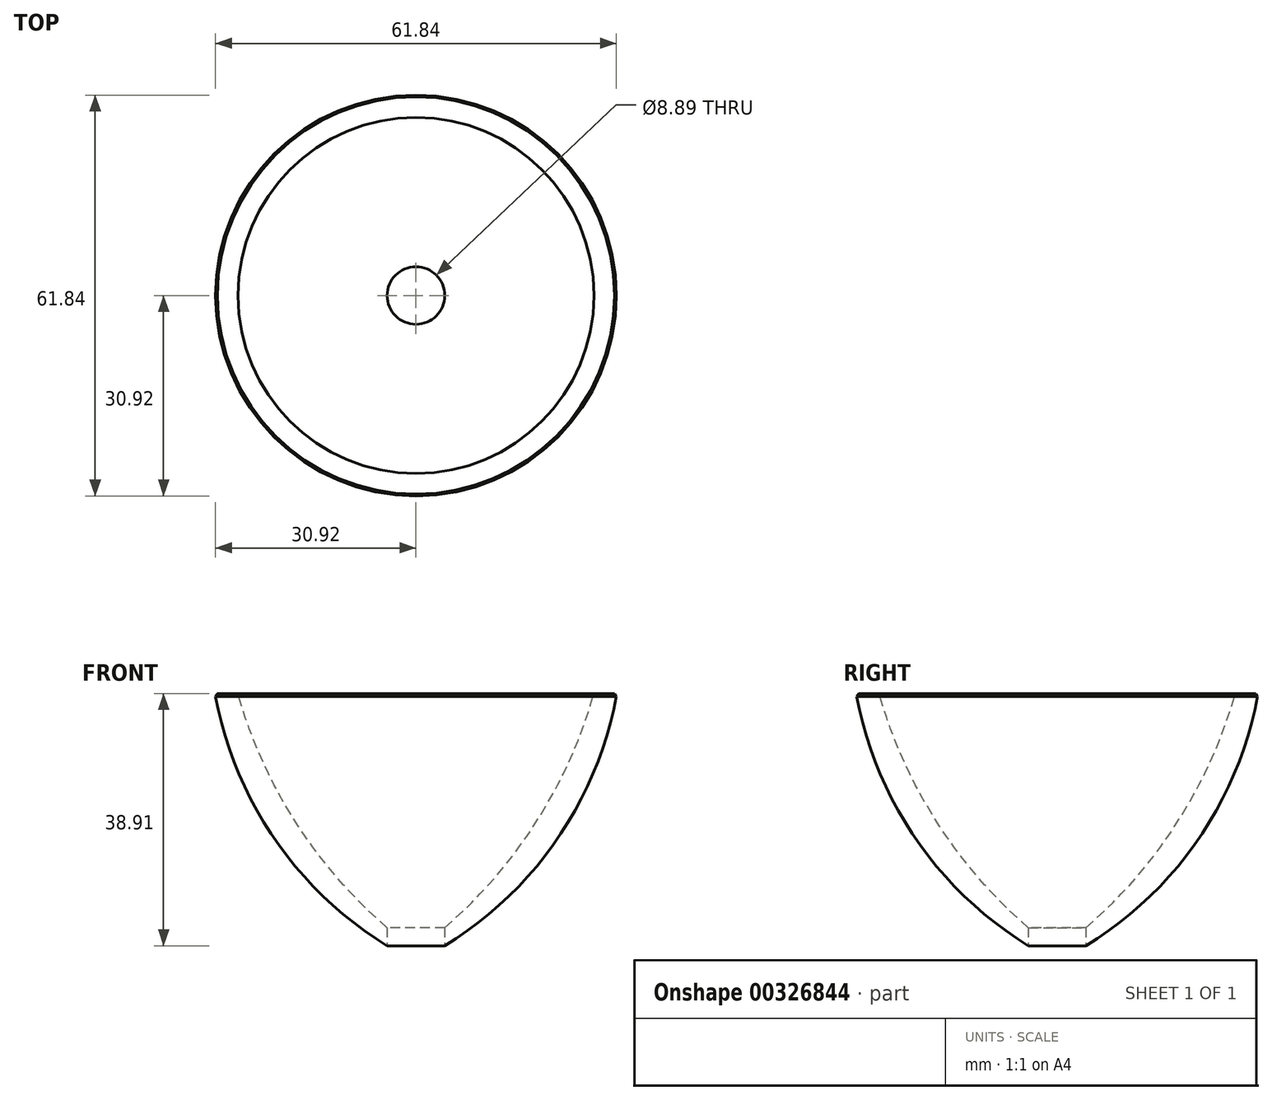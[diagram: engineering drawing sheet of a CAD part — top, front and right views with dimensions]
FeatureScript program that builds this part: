
annotation { "Feature Type Name" : "Feature", "Feature Type Description" : "" }
export const myFeature = defineFeature(function(context is Context, id is Id, definition is map)
    precondition{}
    {
        {
            var Q0;
            Q0=qCreatedBy(makeId("Front.planeOp"),FACE);
            var sketch = newSketch(context, id + "F0", { "sketchPlane" : qUnion([Q0])});
            skLineSegment(sketch, "E0", {"start": v(0, 0) * mm, "end": v(0, 12.7) * mm});
            skLineSegment(sketch, "E1", {"start": v(0, 12.7) * mm, "end": v(3.17, 12.7) * mm});
            skLineSegment(sketch, "E2", {"start": v(3.17, 12.7) * mm, "end": v(3.18, 0) * mm});
            skLineSegment(sketch, "E3", {"start": v(0, 0) * mm, "end": v(3.18, 0) * mm});
            skArc(sketch, "E4", {"start": v(0, 12.7) * mm, "mid": v(17.03, 30.24) * mm, "end": v(27.47, 52.36) * mm});
            skArc(sketch, "E5", {"start": v(3.18, 12.7) * mm, "mid": v(21.35, 29.27) * mm, "end": v(30.92, 51.93) * mm});
            skLineSegment(sketch, "E6", {"start": v(27.47, 52.36) * mm, "end": v(30.64, 52.36) * mm});
            skLineSegment(sketch, "E7", {"start": v(30.64, 52.36) * mm, "end": v(30.92, 51.93) * mm});
            skSolve(sketch);
        }
        {
            var Q0;
            Q0=makeQuery(id+"F0.imprint","IMPRINT",FACE,{"disambiguationData":[TD([[makeQuery(id+"F0.imprint","IMPRINT",EDGE,{"derivedFrom":sQuery(id+"F0.wireOp",EDGE,"E0")}),-1.0]])]});
            var Q1;
            Q1=makeQuery(id+"F0.imprint","IMPRINT",FACE,{"disambiguationData":[TD([[makeQuery(id+"F0.imprint","IMPRINT",EDGE,{"derivedFrom":sQuery(id+"F0.wireOp",EDGE,"E1")}),1.0]])]});
            var Q2;
            Q2=sQuery(id+"F0.wireOp",EDGE,"E0");
            revolve(context, id + "F1", {"entities" : qUnion([Q0, Q1]), "axis" : qUnion([Q2]), "revolveType" : RevolveType.FULL});
        }
        {
            var Q0;
            Q0=makeQuery(id+"F1.opRevolve","SWEPT_FACE",FACE,{"disambiguationData":[OSD([sQuery(id+"F0.wireOp",EDGE,"E3")])]});
            var sketch = newSketch(context, id + "F2", { "sketchPlane" : qUnion([Q0])});
            skCircle(sketch, "E8", {"center": v(0, 0) * mm, "radius": 4.45 * mm});
            skSolve(sketch);
        }
        {
            var Q0;
            Q0 = qSketchRegion(id + "F2", true);
            extrude(context, id + "F3", {"entities" : qUnion([Q0]), "operationType" : NewBodyOperationType.REMOVE, "oppositeDirection" : true, "depth" : 25.4 * mm});
        }
    });
